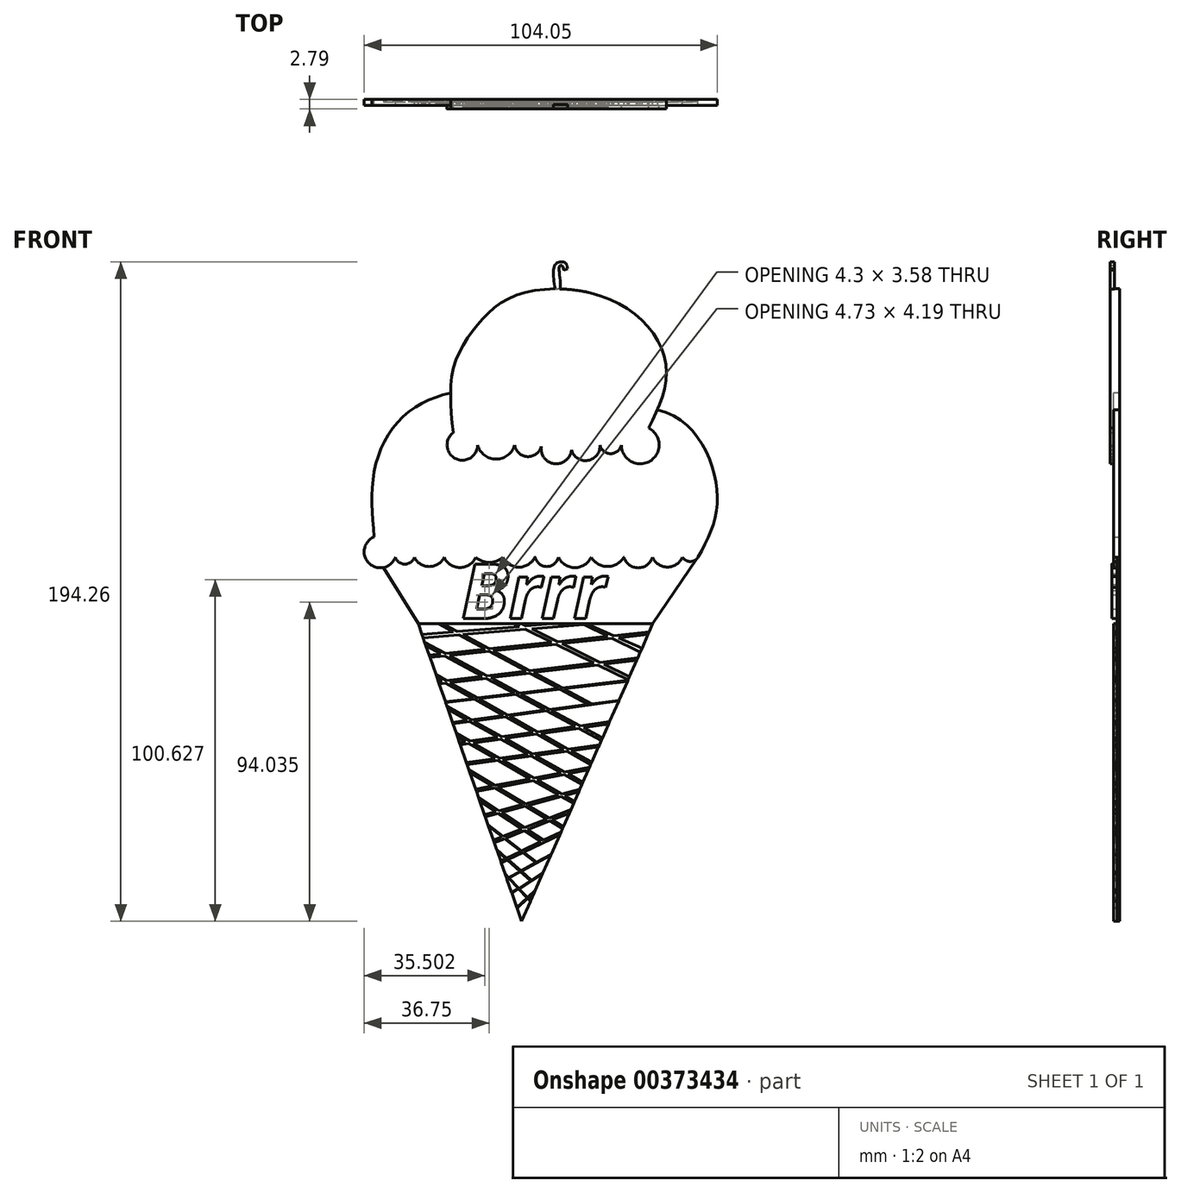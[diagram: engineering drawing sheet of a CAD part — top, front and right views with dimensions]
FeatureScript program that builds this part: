
annotation { "Feature Type Name" : "Feature", "Feature Type Description" : "" }
export const myFeature = defineFeature(function(context is Context, id is Id, definition is map)
    precondition{}
    {
        {
            var Q0;
            Q0=qCreatedBy(makeId("Front.planeOp"),FACE);
            var sketch = newSketch(context, id + "F0", { "sketchPlane" : qUnion([Q0])});
            skLineSegment(sketch, "E0", {"start": v(-30.4, 25.21) * mm, "end": v(0, -62.4) * mm});
            skLineSegment(sketch, "E1", {"start": v(0, -62.4) * mm, "end": v(38.64, 25.21) * mm});
            skLineSegment(sketch, "E2", {"start": v(-30.4, 25.21) * mm, "end": v(38.64, 25.21) * mm});
            skLineSegment(sketch, "E3", {"start": v(-30.4, 25.21) * mm, "end": v(-42.62, 44.84) * mm});
            skLineSegment(sketch, "E4", {"start": v(-42.62, 44.84) * mm, "end": v(51.9, 44.84) * mm});
            skLineSegment(sketch, "E5", {"start": v(51.9, 44.84) * mm, "end": v(38.64, 25.21) * mm});
            skLineSegment(sketch, "E6", {"start": v(-4.74, -48.74) * mm, "end": v(2.58, -56.54) * mm});
            skLineSegment(sketch, "E7", {"start": v(-4.86, -48.38) * mm, "end": v(2.65, -56.4) * mm});
            skLineSegment(sketch, "E8", {"start": v(-7.18, -41.7) * mm, "end": v(4.5, -52.17) * mm});
            skLineSegment(sketch, "E9", {"start": v(-7.38, -41.14) * mm, "end": v(4.5, -51.78) * mm});
            skLineSegment(sketch, "E10", {"start": v(-9.75, -34.3) * mm, "end": v(6.74, -47.12) * mm});
            skLineSegment(sketch, "E11", {"start": v(-9.87, -33.96) * mm, "end": v(6.74, -46.86) * mm});
            skLineSegment(sketch, "E12", {"start": v(-12.3, -26.96) * mm, "end": v(9.29, -41.33) * mm});
            skLineSegment(sketch, "E13", {"start": v(-12.7, -25.8) * mm, "end": v(9.29, -40.44) * mm});
            skLineSegment(sketch, "E14", {"start": v(-15.2, -18.6) * mm, "end": v(12.07, -35.04) * mm});
            skLineSegment(sketch, "E15", {"start": v(-15.46, -17.84) * mm, "end": v(12.27, -34.57) * mm});
            skLineSegment(sketch, "E16", {"start": v(-18.83, -8.15) * mm, "end": v(15.28, -27.74) * mm});
            skLineSegment(sketch, "E17", {"start": v(-19.21, -7.05) * mm, "end": v(15.6, -27.04) * mm});
            skLineSegment(sketch, "E18", {"start": v(-21.66, 0) * mm, "end": v(17.77, -22.1) * mm});
            skLineSegment(sketch, "E19", {"start": v(-22, 1.01) * mm, "end": v(18.06, -21.46) * mm});
            skLineSegment(sketch, "E20", {"start": v(-25.2, 10.22) * mm, "end": v(20.66, -15.56) * mm});
            skLineSegment(sketch, "E21", {"start": v(-28.16, 18.72) * mm, "end": v(23.5, -9.13) * mm});
            skLineSegment(sketch, "E22", {"start": v(-28.54, 19.83) * mm, "end": v(23.81, -8.4) * mm});
            skLineSegment(sketch, "E23", {"start": v(-24.56, 25.21) * mm, "end": v(26.53, -2.24) * mm});
            skLineSegment(sketch, "E24", {"start": v(-23.22, 25.21) * mm, "end": v(26.53, -1.52) * mm});
            skLineSegment(sketch, "E25", {"start": v(-2.21, 25.21) * mm, "end": v(31.38, 8.76) * mm});
            skLineSegment(sketch, "E26", {"start": v(0, 25.21) * mm, "end": v(31.78, 9.65) * mm});
            skLineSegment(sketch, "E27", {"start": v(17.84, 25.21) * mm, "end": v(34.94, 16.83) * mm});
            skLineSegment(sketch, "E28", {"start": v(19.27, 25.21) * mm, "end": v(35.48, 18.06) * mm});
            skLineSegment(sketch, "E29", {"start": v(3.77, -53.84) * mm, "end": v(-1.31, -58.61) * mm});
            skLineSegment(sketch, "E30", {"start": v(4.06, -53.18) * mm, "end": v(-1.41, -58.32) * mm});
            skLineSegment(sketch, "E31", {"start": v(6.21, -48.31) * mm, "end": v(-2.86, -54.17) * mm});
            skLineSegment(sketch, "E32", {"start": v(6.34, -48.03) * mm, "end": v(-2.91, -54) * mm});
            skLineSegment(sketch, "E33", {"start": v(8.6, -42.88) * mm, "end": v(-4.3, -50) * mm});
            skLineSegment(sketch, "E34", {"start": v(8.7, -42.65) * mm, "end": v(-4.35, -49.86) * mm});
            skLineSegment(sketch, "E35", {"start": v(11.6, -36.09) * mm, "end": v(-6.17, -44.6) * mm});
            skLineSegment(sketch, "E36", {"start": v(11.23, -36.94) * mm, "end": v(-6.17, -45.28) * mm});
            skLineSegment(sketch, "E37", {"start": v(14.52, -29.48) * mm, "end": v(-8.3, -38.47) * mm});
            skLineSegment(sketch, "E38", {"start": v(14.02, -30.6) * mm, "end": v(-8.02, -39.28) * mm});
            skLineSegment(sketch, "E39", {"start": v(17.14, -23.52) * mm, "end": v(-10.89, -31.03) * mm});
            skLineSegment(sketch, "E40", {"start": v(16.82, -24.26) * mm, "end": v(-10.89, -31.68) * mm});
            skLineSegment(sketch, "E41", {"start": v(20.35, -16.25) * mm, "end": v(-24.83, 9.14) * mm});
            skLineSegment(sketch, "E42", {"start": v(20, -17.04) * mm, "end": v(-13.5, -23.48) * mm});
            skPoint(sketch, "E42.startSnap0", {"position": v(-1.8, -17.04) * mm});
            skLineSegment(sketch, "E43", {"start": v(19.66, -17.82) * mm, "end": v(-13.5, -24.2) * mm});
            skLineSegment(sketch, "E44", {"start": v(22.92, -10.42) * mm, "end": v(-16.23, -15.63) * mm});
            skLineSegment(sketch, "E45", {"start": v(22.62, -11.11) * mm, "end": v(-16.02, -16.25) * mm});
            skLineSegment(sketch, "E46", {"start": v(25.92, -3.62) * mm, "end": v(-18.28, -9.73) * mm});
            skLineSegment(sketch, "E47", {"start": v(25.6, -4.37) * mm, "end": v(-18.05, -10.4) * mm});
            skLineSegment(sketch, "E48", {"start": v(28.7, 2.7) * mm, "end": v(-20.35, -3.77) * mm});
            skLineSegment(sketch, "E49", {"start": v(-20.18, -4.26) * mm, "end": v(28.61, 2.48) * mm});
            skLineSegment(sketch, "E50", {"start": v(31.17, 8.29) * mm, "end": v(-22.35, 1.98) * mm});
            skLineSegment(sketch, "E51", {"start": v(31.3, 8.57) * mm, "end": v(-22.44, 2.24) * mm});
            skLineSegment(sketch, "E52", {"start": v(34.23, 15.22) * mm, "end": v(-24.5, 8.22) * mm});
            skLineSegment(sketch, "E53", {"start": v(-24.27, 7.53) * mm, "end": v(33.9, 14.47) * mm});
            skLineSegment(sketch, "E54", {"start": v(37.58, 22.81) * mm, "end": v(-27.21, 16) * mm});
            skLineSegment(sketch, "E55", {"start": v(-26.97, 15.3) * mm, "end": v(37.24, 22.04) * mm});
            skLineSegment(sketch, "E56", {"start": v(21.48, 25.21) * mm, "end": v(-28.97, 21.08) * mm});
            skLineSegment(sketch, "E57", {"start": v(-29.32, 22.08) * mm, "end": v(8.91, 25.21) * mm});
            skSolve(sketch);
        }
        {
            var Q0;
            {var subQ0=sQuery(id+"F0.wireOp",EDGE,"E55");var subQ1=sQuery(id+"F0.wireOp",EDGE,"E24");var subQ2=makeQuery(id+"F0.imprint","INTERSECT",VERTEX,{"derivedFrom":[subQ1,subQ0]});Q0=makeQuery(id+"F0.imprint","IMPRINT",FACE,{"disambiguationData":[TD([[makeQuery(id+"F0.imprint","IMPRINT",EDGE,{"disambiguationData":[TD([[subQ2,-1.0]])],"derivedFrom":subQ1}),1.0]])]});}
            var Q1;
            {var subQ0=sQuery(id+"F0.wireOp",EDGE,"E55");var subQ1=sQuery(id+"F0.wireOp",EDGE,"E22");var subQ2=makeQuery(id+"F0.imprint","INTERSECT",VERTEX,{"derivedFrom":[subQ1,subQ0]});Q1=makeQuery(id+"F0.imprint","IMPRINT",FACE,{"disambiguationData":[TD([[makeQuery(id+"F0.imprint","IMPRINT",EDGE,{"disambiguationData":[TD([[subQ2,-1.0]])],"derivedFrom":subQ1}),1.0]])]});}
            var Q2;
            {var subQ0=sQuery(id+"F0.wireOp",EDGE,"E56");var subQ1=sQuery(id+"F0.wireOp",EDGE,"E24");var subQ2=makeQuery(id+"F0.imprint","INTERSECT",VERTEX,{"derivedFrom":[subQ1,subQ0]});Q2=makeQuery(id+"F0.imprint","IMPRINT",FACE,{"disambiguationData":[TD([[makeQuery(id+"F0.imprint","IMPRINT",EDGE,{"disambiguationData":[TD([[subQ2,-1.0]])],"derivedFrom":subQ1}),1.0]])]});}
            var Q3;
            {var subQ1=sQuery(id+"F0.wireOp",EDGE,"E22");var subQ7=sQuery(id+"F0.wireOp",EDGE,"E0");var subQ8=makeQuery(id+"F0.imprint","INTERSECT",VERTEX,{"derivedFrom":[subQ7,subQ1]});Q3=makeQuery(id+"F0.imprint","IMPRINT",FACE,{"disambiguationData":[TD([[makeQuery(id+"F0.imprint","IMPRINT",EDGE,{"disambiguationData":[TD([[subQ8,1.0]])],"derivedFrom":subQ7}),1.0]])]});}
            var Q4;
            {var subQ1=sQuery(id+"F0.wireOp",EDGE,"E1");var subQ7=sQuery(id+"F0.wireOp",EDGE,"E27");var subQ9=makeQuery(id+"F0.imprint","INTERSECT",VERTEX,{"derivedFrom":[subQ1,subQ7]});Q4=makeQuery(id+"F0.imprint","IMPRINT",FACE,{"disambiguationData":[TD([[makeQuery(id+"F0.imprint","IMPRINT",EDGE,{"disambiguationData":[TD([[subQ9,1.0]])],"derivedFrom":subQ1}),1.0]])]});}
            var Q5;
            {var subQ0=sQuery(id+"F0.wireOp",EDGE,"E56");var subQ1=sQuery(id+"F0.wireOp",EDGE,"E26");var subQ2=makeQuery(id+"F0.imprint","INTERSECT",VERTEX,{"derivedFrom":[subQ1,subQ0]});Q5=makeQuery(id+"F0.imprint","IMPRINT",FACE,{"disambiguationData":[TD([[makeQuery(id+"F0.imprint","IMPRINT",EDGE,{"disambiguationData":[TD([[subQ2,-1.0]])],"derivedFrom":subQ1}),1.0]])]});}
            var Q6;
            {var subQ0=sQuery(id+"F0.wireOp",EDGE,"E28");var subQ1=sQuery(id+"F0.wireOp",EDGE,"E1");var subQ2=makeQuery(id+"F0.imprint","INTERSECT",VERTEX,{"derivedFrom":[subQ1,subQ0]});Q6=makeQuery(id+"F0.imprint","IMPRINT",FACE,{"disambiguationData":[TD([[makeQuery(id+"F0.imprint","IMPRINT",EDGE,{"disambiguationData":[TD([[subQ2,-1.0]])],"derivedFrom":subQ1}),1.0]])]});}
            var Q7;
            {var subQ0=sQuery(id+"F0.wireOp",EDGE,"E26");var subQ1=sQuery(id+"F0.wireOp",EDGE,"E1");var subQ2=makeQuery(id+"F0.imprint","INTERSECT",VERTEX,{"derivedFrom":[subQ1,subQ0]});Q7=makeQuery(id+"F0.imprint","IMPRINT",FACE,{"disambiguationData":[TD([[makeQuery(id+"F0.imprint","IMPRINT",EDGE,{"disambiguationData":[TD([[subQ2,-1.0]])],"derivedFrom":subQ1}),1.0]])]});}
            var Q8;
            {var subQ1=sQuery(id+"F0.wireOp",EDGE,"E1");var subQ7=sQuery(id+"F0.wireOp",EDGE,"E25");var subQ9=makeQuery(id+"F0.imprint","INTERSECT",VERTEX,{"derivedFrom":[subQ1,subQ7]});Q8=makeQuery(id+"F0.imprint","IMPRINT",FACE,{"disambiguationData":[TD([[makeQuery(id+"F0.imprint","IMPRINT",EDGE,{"disambiguationData":[TD([[subQ9,1.0]])],"derivedFrom":subQ1}),1.0]])]});}
            var Q9;
            {var subQ0=sQuery(id+"F0.wireOp",EDGE,"E48");var subQ1=sQuery(id+"F0.wireOp",EDGE,"E1");var subQ2=makeQuery(id+"F0.imprint","INTERSECT",VERTEX,{"derivedFrom":[subQ1,subQ0]});Q9=makeQuery(id+"F0.imprint","IMPRINT",FACE,{"disambiguationData":[TD([[makeQuery(id+"F0.imprint","IMPRINT",EDGE,{"disambiguationData":[TD([[subQ2,-1.0]])],"derivedFrom":subQ1}),1.0]])]});}
            var Q10;
            {var subQ0=sQuery(id+"F0.wireOp",EDGE,"E50");var subQ1=sQuery(id+"F0.wireOp",EDGE,"E22");var subQ2=makeQuery(id+"F0.imprint","INTERSECT",VERTEX,{"derivedFrom":[subQ1,subQ0]});Q10=makeQuery(id+"F0.imprint","IMPRINT",FACE,{"disambiguationData":[TD([[makeQuery(id+"F0.imprint","IMPRINT",EDGE,{"disambiguationData":[TD([[subQ2,-1.0]])],"derivedFrom":subQ1}),1.0]])]});}
            var Q11;
            {var subQ0=sQuery(id+"F0.wireOp",EDGE,"E53");var subQ1=sQuery(id+"F0.wireOp",EDGE,"E22");var subQ2=makeQuery(id+"F0.imprint","INTERSECT",VERTEX,{"derivedFrom":[subQ1,subQ0]});Q11=makeQuery(id+"F0.imprint","IMPRINT",FACE,{"disambiguationData":[TD([[makeQuery(id+"F0.imprint","IMPRINT",EDGE,{"disambiguationData":[TD([[subQ2,-1.0]])],"derivedFrom":subQ1}),1.0]])]});}
            var Q12;
            {var subQ0=sQuery(id+"F0.wireOp",EDGE,"E53");var subQ1=sQuery(id+"F0.wireOp",EDGE,"E20");var subQ2=makeQuery(id+"F0.imprint","INTERSECT",VERTEX,{"derivedFrom":[subQ1,subQ0]});Q12=makeQuery(id+"F0.imprint","IMPRINT",FACE,{"disambiguationData":[TD([[makeQuery(id+"F0.imprint","IMPRINT",EDGE,{"disambiguationData":[TD([[subQ2,-1.0]])],"derivedFrom":subQ1}),1.0]])]});}
            var Q13;
            {var subQ0=sQuery(id+"F0.wireOp",EDGE,"E50");var subQ1=sQuery(id+"F0.wireOp",EDGE,"E20");var subQ2=makeQuery(id+"F0.imprint","INTERSECT",VERTEX,{"derivedFrom":[subQ1,subQ0]});Q13=makeQuery(id+"F0.imprint","IMPRINT",FACE,{"disambiguationData":[TD([[makeQuery(id+"F0.imprint","IMPRINT",EDGE,{"disambiguationData":[TD([[subQ2,-1.0]])],"derivedFrom":subQ1}),1.0]])]});}
            var Q14;
            {var subQ0=sQuery(id+"F0.wireOp",EDGE,"E49");var subQ1=sQuery(id+"F0.wireOp",EDGE,"E20");var subQ2=makeQuery(id+"F0.imprint","INTERSECT",VERTEX,{"derivedFrom":[subQ1,subQ0]});Q14=makeQuery(id+"F0.imprint","IMPRINT",FACE,{"disambiguationData":[TD([[makeQuery(id+"F0.imprint","IMPRINT",EDGE,{"disambiguationData":[TD([[subQ2,-1.0]])],"derivedFrom":subQ1}),1.0]])]});}
            var Q15;
            {var subQ1=sQuery(id+"F0.wireOp",EDGE,"E1");var subQ7=sQuery(id+"F0.wireOp",EDGE,"E23");var subQ9=makeQuery(id+"F0.imprint","INTERSECT",VERTEX,{"derivedFrom":[subQ1,subQ7]});Q15=makeQuery(id+"F0.imprint","IMPRINT",FACE,{"disambiguationData":[TD([[makeQuery(id+"F0.imprint","IMPRINT",EDGE,{"disambiguationData":[TD([[subQ9,1.0]])],"derivedFrom":subQ1}),1.0]])]});}
            var Q16;
            {var subQ0=sQuery(id+"F0.wireOp",EDGE,"E21");var subQ1=sQuery(id+"F0.wireOp",EDGE,"E1");var subQ2=makeQuery(id+"F0.imprint","INTERSECT",VERTEX,{"derivedFrom":[subQ1,subQ0]});Q16=makeQuery(id+"F0.imprint","IMPRINT",FACE,{"disambiguationData":[TD([[makeQuery(id+"F0.imprint","IMPRINT",EDGE,{"disambiguationData":[TD([[subQ2,1.0]])],"derivedFrom":subQ1}),1.0]])]});}
            var Q17;
            {var subQ0=sQuery(id+"F0.wireOp",EDGE,"E47");var subQ1=sQuery(id+"F0.wireOp",EDGE,"E19");var subQ2=makeQuery(id+"F0.imprint","INTERSECT",VERTEX,{"derivedFrom":[subQ1,subQ0]});Q17=makeQuery(id+"F0.imprint","IMPRINT",FACE,{"disambiguationData":[TD([[makeQuery(id+"F0.imprint","IMPRINT",EDGE,{"disambiguationData":[TD([[subQ2,-1.0]])],"derivedFrom":subQ1}),1.0]])]});}
            var Q18;
            {var subQ0=sQuery(id+"F0.wireOp",EDGE,"E49");var subQ1=sQuery(id+"F0.wireOp",EDGE,"E19");var subQ2=makeQuery(id+"F0.imprint","INTERSECT",VERTEX,{"derivedFrom":[subQ1,subQ0]});Q18=makeQuery(id+"F0.imprint","IMPRINT",FACE,{"disambiguationData":[TD([[makeQuery(id+"F0.imprint","IMPRINT",EDGE,{"disambiguationData":[TD([[subQ2,-1.0]])],"derivedFrom":subQ1}),1.0]])]});}
            var Q19;
            {var subQ5=sQuery(id+"F0.wireOp",EDGE,"E19");var subQ7=sQuery(id+"F0.wireOp",EDGE,"E0");var subQ8=makeQuery(id+"F0.imprint","INTERSECT",VERTEX,{"derivedFrom":[subQ7,subQ5]});Q19=makeQuery(id+"F0.imprint","IMPRINT",FACE,{"disambiguationData":[TD([[makeQuery(id+"F0.imprint","IMPRINT",EDGE,{"disambiguationData":[TD([[subQ8,1.0]])],"derivedFrom":subQ7}),1.0]])]});}
            var Q20;
            {var subQ5=sQuery(id+"F0.wireOp",EDGE,"E17");var subQ7=sQuery(id+"F0.wireOp",EDGE,"E0");var subQ8=makeQuery(id+"F0.imprint","INTERSECT",VERTEX,{"derivedFrom":[subQ7,subQ5]});Q20=makeQuery(id+"F0.imprint","IMPRINT",FACE,{"disambiguationData":[TD([[makeQuery(id+"F0.imprint","IMPRINT",EDGE,{"disambiguationData":[TD([[subQ8,1.0]])],"derivedFrom":subQ7}),1.0]])]});}
            var Q21;
            {var subQ0=sQuery(id+"F0.wireOp",EDGE,"E47");var subQ1=sQuery(id+"F0.wireOp",EDGE,"E17");var subQ2=makeQuery(id+"F0.imprint","INTERSECT",VERTEX,{"derivedFrom":[subQ1,subQ0]});Q21=makeQuery(id+"F0.imprint","IMPRINT",FACE,{"disambiguationData":[TD([[makeQuery(id+"F0.imprint","IMPRINT",EDGE,{"disambiguationData":[TD([[subQ2,-1.0]])],"derivedFrom":subQ1}),1.0]])]});}
            var Q22;
            {var subQ0=sQuery(id+"F0.wireOp",EDGE,"E45");var subQ1=sQuery(id+"F0.wireOp",EDGE,"E17");var subQ2=makeQuery(id+"F0.imprint","INTERSECT",VERTEX,{"derivedFrom":[subQ1,subQ0]});Q22=makeQuery(id+"F0.imprint","IMPRINT",FACE,{"disambiguationData":[TD([[makeQuery(id+"F0.imprint","IMPRINT",EDGE,{"disambiguationData":[TD([[subQ2,-1.0]])],"derivedFrom":subQ1}),1.0]])]});}
            var Q23;
            {var subQ1=sQuery(id+"F0.wireOp",EDGE,"E1");var subQ5=sQuery(id+"F0.wireOp",EDGE,"E41");var subQ6=makeQuery(id+"F0.imprint","INTERSECT",VERTEX,{"derivedFrom":[subQ1,subQ5]});Q23=makeQuery(id+"F0.imprint","IMPRINT",FACE,{"disambiguationData":[TD([[makeQuery(id+"F0.imprint","IMPRINT",EDGE,{"disambiguationData":[TD([[subQ6,1.0]])],"derivedFrom":subQ1}),1.0]])]});}
            var Q24;
            {var subQ0=sQuery(id+"F0.wireOp",EDGE,"E18");var subQ1=sQuery(id+"F0.wireOp",EDGE,"E1");var subQ2=makeQuery(id+"F0.imprint","INTERSECT",VERTEX,{"derivedFrom":[subQ1,subQ0]});Q24=makeQuery(id+"F0.imprint","IMPRINT",FACE,{"disambiguationData":[TD([[makeQuery(id+"F0.imprint","IMPRINT",EDGE,{"disambiguationData":[TD([[subQ2,1.0]])],"derivedFrom":subQ1}),1.0]])]});}
            var Q25;
            {var subQ0=sQuery(id+"F0.wireOp",EDGE,"E43");var subQ1=sQuery(id+"F0.wireOp",EDGE,"E15");var subQ2=makeQuery(id+"F0.imprint","INTERSECT",VERTEX,{"derivedFrom":[subQ1,subQ0]});Q25=makeQuery(id+"F0.imprint","IMPRINT",FACE,{"disambiguationData":[TD([[makeQuery(id+"F0.imprint","IMPRINT",EDGE,{"disambiguationData":[TD([[subQ2,-1.0]])],"derivedFrom":subQ1}),1.0]])]});}
            var Q26;
            {var subQ1=sQuery(id+"F0.wireOp",EDGE,"E13");var subQ5=sQuery(id+"F0.wireOp",EDGE,"E0");var subQ6=makeQuery(id+"F0.imprint","INTERSECT",VERTEX,{"derivedFrom":[subQ5,subQ1]});Q26=makeQuery(id+"F0.imprint","IMPRINT",FACE,{"disambiguationData":[TD([[makeQuery(id+"F0.imprint","IMPRINT",EDGE,{"disambiguationData":[TD([[subQ6,1.0]])],"derivedFrom":subQ5}),1.0]])]});}
            var Q27;
            {var subQ0=sQuery(id+"F0.wireOp",EDGE,"E15");var subQ1=sQuery(id+"F0.wireOp",EDGE,"E0");var subQ2=makeQuery(id+"F0.imprint","INTERSECT",VERTEX,{"derivedFrom":[subQ1,subQ0]});Q27=makeQuery(id+"F0.imprint","IMPRINT",FACE,{"disambiguationData":[TD([[makeQuery(id+"F0.imprint","IMPRINT",EDGE,{"disambiguationData":[TD([[subQ2,1.0]])],"derivedFrom":subQ1}),1.0]])]});}
            var Q28;
            {var subQ0=sQuery(id+"F0.wireOp",EDGE,"E40");var subQ1=sQuery(id+"F0.wireOp",EDGE,"E13");var subQ2=makeQuery(id+"F0.imprint","INTERSECT",VERTEX,{"derivedFrom":[subQ1,subQ0]});Q28=makeQuery(id+"F0.imprint","IMPRINT",FACE,{"disambiguationData":[TD([[makeQuery(id+"F0.imprint","IMPRINT",EDGE,{"disambiguationData":[TD([[subQ2,-1.0]])],"derivedFrom":subQ1}),1.0]])]});}
            var Q29;
            {var subQ0=sQuery(id+"F0.wireOp",EDGE,"E16");var subQ1=sQuery(id+"F0.wireOp",EDGE,"E1");var subQ2=makeQuery(id+"F0.imprint","INTERSECT",VERTEX,{"derivedFrom":[subQ1,subQ0]});Q29=makeQuery(id+"F0.imprint","IMPRINT",FACE,{"disambiguationData":[TD([[makeQuery(id+"F0.imprint","IMPRINT",EDGE,{"disambiguationData":[TD([[subQ2,1.0]])],"derivedFrom":subQ1}),1.0]])]});}
            var Q30;
            {var subQ5=sQuery(id+"F0.wireOp",EDGE,"E1");var subQ7=sQuery(id+"F0.wireOp",EDGE,"E14");var subQ8=makeQuery(id+"F0.imprint","INTERSECT",VERTEX,{"derivedFrom":[subQ5,subQ7]});Q30=makeQuery(id+"F0.imprint","IMPRINT",FACE,{"disambiguationData":[TD([[makeQuery(id+"F0.imprint","IMPRINT",EDGE,{"disambiguationData":[TD([[subQ8,1.0]])],"derivedFrom":subQ5}),1.0]])]});}
            var Q31;
            {var subQ0=sQuery(id+"F0.wireOp",EDGE,"E38");var subQ1=sQuery(id+"F0.wireOp",EDGE,"E11");var subQ2=makeQuery(id+"F0.imprint","INTERSECT",VERTEX,{"derivedFrom":[subQ1,subQ0]});Q31=makeQuery(id+"F0.imprint","IMPRINT",FACE,{"disambiguationData":[TD([[makeQuery(id+"F0.imprint","IMPRINT",EDGE,{"disambiguationData":[TD([[subQ2,-1.0]])],"derivedFrom":subQ1}),1.0]])]});}
            var Q32;
            {var subQ1=sQuery(id+"F0.wireOp",EDGE,"E11");var subQ7=sQuery(id+"F0.wireOp",EDGE,"E0");var subQ8=makeQuery(id+"F0.imprint","INTERSECT",VERTEX,{"derivedFrom":[subQ7,subQ1]});Q32=makeQuery(id+"F0.imprint","IMPRINT",FACE,{"disambiguationData":[TD([[makeQuery(id+"F0.imprint","IMPRINT",EDGE,{"disambiguationData":[TD([[subQ8,1.0]])],"derivedFrom":subQ7}),1.0]])]});}
            var Q33;
            {var subQ5=sQuery(id+"F0.wireOp",EDGE,"E9");var subQ6=sQuery(id+"F0.wireOp",EDGE,"E0");var subQ7=makeQuery(id+"F0.imprint","INTERSECT",VERTEX,{"derivedFrom":[subQ6,subQ5]});Q33=makeQuery(id+"F0.imprint","IMPRINT",FACE,{"disambiguationData":[TD([[makeQuery(id+"F0.imprint","IMPRINT",EDGE,{"disambiguationData":[TD([[subQ7,1.0]])],"derivedFrom":subQ6}),1.0]])]});}
            var Q34;
            {var subQ1=sQuery(id+"F0.wireOp",EDGE,"E1");var subQ7=sQuery(id+"F0.wireOp",EDGE,"E12");var subQ8=makeQuery(id+"F0.imprint","INTERSECT",VERTEX,{"derivedFrom":[subQ1,subQ7]});Q34=makeQuery(id+"F0.imprint","IMPRINT",FACE,{"disambiguationData":[TD([[makeQuery(id+"F0.imprint","IMPRINT",EDGE,{"disambiguationData":[TD([[subQ8,1.0]])],"derivedFrom":subQ1}),1.0]])]});}
            var Q35;
            {var subQ0=sQuery(id+"F0.wireOp",EDGE,"E36");var subQ1=sQuery(id+"F0.wireOp",EDGE,"E9");var subQ2=makeQuery(id+"F0.imprint","INTERSECT",VERTEX,{"derivedFrom":[subQ1,subQ0]});Q35=makeQuery(id+"F0.imprint","IMPRINT",FACE,{"disambiguationData":[TD([[makeQuery(id+"F0.imprint","IMPRINT",EDGE,{"disambiguationData":[TD([[subQ2,-1.0]])],"derivedFrom":subQ1}),1.0]])]});}
            var Q36;
            {var subQ1=sQuery(id+"F0.wireOp",EDGE,"E1");var subQ7=sQuery(id+"F0.wireOp",EDGE,"E10");var subQ8=makeQuery(id+"F0.imprint","INTERSECT",VERTEX,{"derivedFrom":[subQ1,subQ7]});Q36=makeQuery(id+"F0.imprint","IMPRINT",FACE,{"disambiguationData":[TD([[makeQuery(id+"F0.imprint","IMPRINT",EDGE,{"disambiguationData":[TD([[subQ8,1.0]])],"derivedFrom":subQ1}),1.0]])]});}
            var Q37;
            {var subQ0=sQuery(id+"F0.wireOp",EDGE,"E33");var subQ1=sQuery(id+"F0.wireOp",EDGE,"E7");var subQ2=makeQuery(id+"F0.imprint","INTERSECT",VERTEX,{"derivedFrom":[subQ1,subQ0]});Q37=makeQuery(id+"F0.imprint","IMPRINT",FACE,{"disambiguationData":[TD([[makeQuery(id+"F0.imprint","IMPRINT",EDGE,{"disambiguationData":[TD([[subQ2,-1.0]])],"derivedFrom":subQ1}),1.0]])]});}
            var Q38;
            {var subQ1=sQuery(id+"F0.wireOp",EDGE,"E1");var subQ7=sQuery(id+"F0.wireOp",EDGE,"E8");var subQ8=makeQuery(id+"F0.imprint","INTERSECT",VERTEX,{"derivedFrom":[subQ1,subQ7]});Q38=makeQuery(id+"F0.imprint","IMPRINT",FACE,{"disambiguationData":[TD([[makeQuery(id+"F0.imprint","IMPRINT",EDGE,{"disambiguationData":[TD([[subQ8,1.0]])],"derivedFrom":subQ1}),1.0]])]});}
            var Q39;
            {var subQ0=sQuery(id+"F0.wireOp",EDGE,"E30");var subQ1=sQuery(id+"F0.wireOp",EDGE,"E0");var subQ2=makeQuery(id+"F0.imprint","INTERSECT",VERTEX,{"derivedFrom":[subQ1,subQ0]});Q39=makeQuery(id+"F0.imprint","IMPRINT",FACE,{"disambiguationData":[TD([[makeQuery(id+"F0.imprint","IMPRINT",EDGE,{"disambiguationData":[TD([[subQ2,1.0]])],"derivedFrom":subQ1}),1.0]])]});}
            var Q40;
            {var subQ0=sQuery(id+"F0.wireOp",EDGE,"E1");var subQ1=sQuery(id+"F0.wireOp",EDGE,"E0");var subQ2=makeQuery(id+"F0.imprint","INTERSECT",VERTEX,{"derivedFrom":[subQ1,subQ0]});Q40=makeQuery(id+"F0.imprint","IMPRINT",FACE,{"disambiguationData":[TD([[makeQuery(id+"F0.imprint","IMPRINT",EDGE,{"disambiguationData":[TD([[subQ2,1.0]])],"derivedFrom":subQ1}),1.0]])]});}
            var Q41;
            {var subQ0=sQuery(id+"F0.wireOp",EDGE,"E44");var subQ1=sQuery(id+"F0.wireOp",EDGE,"E0");var subQ2=makeQuery(id+"F0.imprint","INTERSECT",VERTEX,{"derivedFrom":[subQ1,subQ0]});Q41=makeQuery(id+"F0.imprint","IMPRINT",FACE,{"disambiguationData":[TD([[makeQuery(id+"F0.imprint","IMPRINT",EDGE,{"disambiguationData":[TD([[subQ2,1.0]])],"derivedFrom":subQ1}),1.0]])]});}
            var Q42;
            {var subQ0=sQuery(id+"F0.wireOp",EDGE,"E18");var subQ1=sQuery(id+"F0.wireOp",EDGE,"E0");var subQ2=makeQuery(id+"F0.imprint","INTERSECT",VERTEX,{"derivedFrom":[subQ1,subQ0]});Q42=makeQuery(id+"F0.imprint","IMPRINT",FACE,{"disambiguationData":[TD([[makeQuery(id+"F0.imprint","IMPRINT",EDGE,{"disambiguationData":[TD([[subQ2,-1.0]])],"derivedFrom":subQ1}),1.0]])]});}
            var Q43;
            {var subQ0=sQuery(id+"F0.wireOp",EDGE,"E51");var subQ1=sQuery(id+"F0.wireOp",EDGE,"E0");var subQ2=makeQuery(id+"F0.imprint","INTERSECT",VERTEX,{"derivedFrom":[subQ1,subQ0]});Q43=makeQuery(id+"F0.imprint","IMPRINT",FACE,{"disambiguationData":[TD([[makeQuery(id+"F0.imprint","IMPRINT",EDGE,{"disambiguationData":[TD([[subQ2,1.0]])],"derivedFrom":subQ1}),1.0]])]});}
            var Q44;
            {var subQ1=sQuery(id+"F0.wireOp",EDGE,"E20");var subQ7=sQuery(id+"F0.wireOp",EDGE,"E0");var subQ8=makeQuery(id+"F0.imprint","INTERSECT",VERTEX,{"derivedFrom":[subQ7,subQ1]});Q44=makeQuery(id+"F0.imprint","IMPRINT",FACE,{"disambiguationData":[TD([[makeQuery(id+"F0.imprint","IMPRINT",EDGE,{"disambiguationData":[TD([[subQ8,1.0]])],"derivedFrom":subQ7}),1.0]])]});}
            var Q45;
            {var subQ0=sQuery(id+"F0.wireOp",EDGE,"E24");var subQ1=sQuery(id+"F0.wireOp",EDGE,"E2");var subQ2=makeQuery(id+"F0.imprint","INTERSECT",VERTEX,{"derivedFrom":[subQ1,subQ0]});Q45=makeQuery(id+"F0.imprint","IMPRINT",FACE,{"disambiguationData":[TD([[makeQuery(id+"F0.imprint","IMPRINT",EDGE,{"disambiguationData":[TD([[subQ2,-1.0]])],"derivedFrom":subQ1}),-1.0]])]});}
            var Q46;
            {var subQ3=sQuery(id+"F0.wireOp",EDGE,"E28");var subQ5=sQuery(id+"F0.wireOp",EDGE,"E56");var subQ6=makeQuery(id+"F0.imprint","INTERSECT",VERTEX,{"derivedFrom":[subQ3,subQ5]});Q46=makeQuery(id+"F0.imprint","IMPRINT",FACE,{"disambiguationData":[TD([[makeQuery(id+"F0.imprint","IMPRINT",EDGE,{"disambiguationData":[TD([[subQ6,-1.0]])],"derivedFrom":subQ3}),1.0]])]});}
            var Q47;
            {var subQ0=sQuery(id+"F0.wireOp",EDGE,"E23");var subQ1=sQuery(id+"F0.wireOp",EDGE,"E1");var subQ2=makeQuery(id+"F0.imprint","INTERSECT",VERTEX,{"derivedFrom":[subQ1,subQ0]});Q47=makeQuery(id+"F0.imprint","IMPRINT",FACE,{"disambiguationData":[TD([[makeQuery(id+"F0.imprint","IMPRINT",EDGE,{"disambiguationData":[TD([[subQ2,-1.0]])],"derivedFrom":subQ1}),1.0]])]});}
            var Q48;
            {var subQ0=sQuery(id+"F0.wireOp",EDGE,"E22");var subQ1=sQuery(id+"F0.wireOp",EDGE,"E1");var subQ2=makeQuery(id+"F0.imprint","INTERSECT",VERTEX,{"derivedFrom":[subQ1,subQ0]});Q48=makeQuery(id+"F0.imprint","IMPRINT",FACE,{"disambiguationData":[TD([[makeQuery(id+"F0.imprint","IMPRINT",EDGE,{"disambiguationData":[TD([[subQ2,-1.0]])],"derivedFrom":subQ1}),1.0]])]});}
            var Q49;
            {var subQ0=sQuery(id+"F0.wireOp",EDGE,"E20");var subQ1=sQuery(id+"F0.wireOp",EDGE,"E1");var subQ2=makeQuery(id+"F0.imprint","INTERSECT",VERTEX,{"derivedFrom":[subQ1,subQ0]});Q49=makeQuery(id+"F0.imprint","IMPRINT",FACE,{"disambiguationData":[TD([[makeQuery(id+"F0.imprint","IMPRINT",EDGE,{"disambiguationData":[TD([[subQ2,-1.0]])],"derivedFrom":subQ1}),1.0]])]});}
            var Q50;
            {var subQ0=sQuery(id+"F0.wireOp",EDGE,"E19");var subQ1=sQuery(id+"F0.wireOp",EDGE,"E1");var subQ2=makeQuery(id+"F0.imprint","INTERSECT",VERTEX,{"derivedFrom":[subQ1,subQ0]});Q50=makeQuery(id+"F0.imprint","IMPRINT",FACE,{"disambiguationData":[TD([[makeQuery(id+"F0.imprint","IMPRINT",EDGE,{"disambiguationData":[TD([[subQ2,-1.0]])],"derivedFrom":subQ1}),1.0]])]});}
            var Q51;
            {var subQ0=sQuery(id+"F0.wireOp",EDGE,"E17");var subQ1=sQuery(id+"F0.wireOp",EDGE,"E1");var subQ2=makeQuery(id+"F0.imprint","INTERSECT",VERTEX,{"derivedFrom":[subQ1,subQ0]});Q51=makeQuery(id+"F0.imprint","IMPRINT",FACE,{"disambiguationData":[TD([[makeQuery(id+"F0.imprint","IMPRINT",EDGE,{"disambiguationData":[TD([[subQ2,-1.0]])],"derivedFrom":subQ1}),1.0]])]});}
            var Q52;
            {var subQ0=sQuery(id+"F0.wireOp",EDGE,"E15");var subQ1=sQuery(id+"F0.wireOp",EDGE,"E1");var subQ2=makeQuery(id+"F0.imprint","INTERSECT",VERTEX,{"derivedFrom":[subQ1,subQ0]});Q52=makeQuery(id+"F0.imprint","IMPRINT",FACE,{"disambiguationData":[TD([[makeQuery(id+"F0.imprint","IMPRINT",EDGE,{"disambiguationData":[TD([[subQ2,-1.0]])],"derivedFrom":subQ1}),1.0]])]});}
            var Q53;
            {var subQ0=sQuery(id+"F0.wireOp",EDGE,"E12");var subQ1=sQuery(id+"F0.wireOp",EDGE,"E1");var subQ2=makeQuery(id+"F0.imprint","INTERSECT",VERTEX,{"derivedFrom":[subQ1,subQ0]});Q53=makeQuery(id+"F0.imprint","IMPRINT",FACE,{"disambiguationData":[TD([[makeQuery(id+"F0.imprint","IMPRINT",EDGE,{"disambiguationData":[TD([[subQ2,-1.0]])],"derivedFrom":subQ1}),1.0]])]});}
            var Q54;
            {var subQ0=sQuery(id+"F0.wireOp",EDGE,"E10");var subQ1=sQuery(id+"F0.wireOp",EDGE,"E1");var subQ2=makeQuery(id+"F0.imprint","INTERSECT",VERTEX,{"derivedFrom":[subQ1,subQ0]});Q54=makeQuery(id+"F0.imprint","IMPRINT",FACE,{"disambiguationData":[TD([[makeQuery(id+"F0.imprint","IMPRINT",EDGE,{"disambiguationData":[TD([[subQ2,-1.0]])],"derivedFrom":subQ1}),1.0]])]});}
            var Q55;
            {var subQ0=sQuery(id+"F0.wireOp",EDGE,"E8");var subQ1=sQuery(id+"F0.wireOp",EDGE,"E1");var subQ2=makeQuery(id+"F0.imprint","INTERSECT",VERTEX,{"derivedFrom":[subQ1,subQ0]});Q55=makeQuery(id+"F0.imprint","IMPRINT",FACE,{"disambiguationData":[TD([[makeQuery(id+"F0.imprint","IMPRINT",EDGE,{"disambiguationData":[TD([[subQ2,-1.0]])],"derivedFrom":subQ1}),1.0]])]});}
            var Q56;
            {var subQ0=sQuery(id+"F0.wireOp",EDGE,"E7");var subQ1=sQuery(id+"F0.wireOp",EDGE,"E1");var subQ2=makeQuery(id+"F0.imprint","INTERSECT",VERTEX,{"derivedFrom":[subQ1,subQ0]});Q56=makeQuery(id+"F0.imprint","IMPRINT",FACE,{"disambiguationData":[TD([[makeQuery(id+"F0.imprint","IMPRINT",EDGE,{"disambiguationData":[TD([[subQ2,-1.0]])],"derivedFrom":subQ1}),1.0]])]});}
            var Q57;
            {var subQ0=sQuery(id+"F0.wireOp",EDGE,"E32");var subQ1=sQuery(id+"F0.wireOp",EDGE,"E0");var subQ2=makeQuery(id+"F0.imprint","INTERSECT",VERTEX,{"derivedFrom":[subQ1,subQ0]});Q57=makeQuery(id+"F0.imprint","IMPRINT",FACE,{"disambiguationData":[TD([[makeQuery(id+"F0.imprint","IMPRINT",EDGE,{"disambiguationData":[TD([[subQ2,1.0]])],"derivedFrom":subQ1}),1.0]])]});}
            var Q58;
            {var subQ0=sQuery(id+"F0.wireOp",EDGE,"E6");var subQ1=sQuery(id+"F0.wireOp",EDGE,"E0");var subQ2=makeQuery(id+"F0.imprint","INTERSECT",VERTEX,{"derivedFrom":[subQ1,subQ0]});Q58=makeQuery(id+"F0.imprint","IMPRINT",FACE,{"disambiguationData":[TD([[makeQuery(id+"F0.imprint","IMPRINT",EDGE,{"disambiguationData":[TD([[subQ2,-1.0]])],"derivedFrom":subQ1}),1.0]])]});}
            var Q59;
            {var subQ1=sQuery(id+"F0.wireOp",EDGE,"E7");var subQ7=sQuery(id+"F0.wireOp",EDGE,"E0");var subQ8=makeQuery(id+"F0.imprint","INTERSECT",VERTEX,{"derivedFrom":[subQ7,subQ1]});Q59=makeQuery(id+"F0.imprint","IMPRINT",FACE,{"disambiguationData":[TD([[makeQuery(id+"F0.imprint","IMPRINT",EDGE,{"disambiguationData":[TD([[subQ8,1.0]])],"derivedFrom":subQ7}),1.0]])]});}
            var Q60;
            {var subQ0=sQuery(id+"F0.wireOp",EDGE,"E8");var subQ1=sQuery(id+"F0.wireOp",EDGE,"E0");var subQ2=makeQuery(id+"F0.imprint","INTERSECT",VERTEX,{"derivedFrom":[subQ1,subQ0]});Q60=makeQuery(id+"F0.imprint","IMPRINT",FACE,{"disambiguationData":[TD([[makeQuery(id+"F0.imprint","IMPRINT",EDGE,{"disambiguationData":[TD([[subQ2,-1.0]])],"derivedFrom":subQ1}),1.0]])]});}
            var Q61;
            {var subQ0=sQuery(id+"F0.wireOp",EDGE,"E10");var subQ1=sQuery(id+"F0.wireOp",EDGE,"E0");var subQ2=makeQuery(id+"F0.imprint","INTERSECT",VERTEX,{"derivedFrom":[subQ1,subQ0]});Q61=makeQuery(id+"F0.imprint","IMPRINT",FACE,{"disambiguationData":[TD([[makeQuery(id+"F0.imprint","IMPRINT",EDGE,{"disambiguationData":[TD([[subQ2,-1.0]])],"derivedFrom":subQ1}),1.0]])]});}
            var Q62;
            {var subQ0=sQuery(id+"F0.wireOp",EDGE,"E12");var subQ1=sQuery(id+"F0.wireOp",EDGE,"E0");var subQ2=makeQuery(id+"F0.imprint","INTERSECT",VERTEX,{"derivedFrom":[subQ1,subQ0]});Q62=makeQuery(id+"F0.imprint","IMPRINT",FACE,{"disambiguationData":[TD([[makeQuery(id+"F0.imprint","IMPRINT",EDGE,{"disambiguationData":[TD([[subQ2,-1.0]])],"derivedFrom":subQ1}),1.0]])]});}
            var Q63;
            {var subQ0=sQuery(id+"F0.wireOp",EDGE,"E14");var subQ1=sQuery(id+"F0.wireOp",EDGE,"E0");var subQ2=makeQuery(id+"F0.imprint","INTERSECT",VERTEX,{"derivedFrom":[subQ1,subQ0]});Q63=makeQuery(id+"F0.imprint","IMPRINT",FACE,{"disambiguationData":[TD([[makeQuery(id+"F0.imprint","IMPRINT",EDGE,{"disambiguationData":[TD([[subQ2,-1.0]])],"derivedFrom":subQ1}),1.0]])]});}
            var Q64;
            {var subQ0=sQuery(id+"F0.wireOp",EDGE,"E16");var subQ1=sQuery(id+"F0.wireOp",EDGE,"E0");var subQ2=makeQuery(id+"F0.imprint","INTERSECT",VERTEX,{"derivedFrom":[subQ1,subQ0]});Q64=makeQuery(id+"F0.imprint","IMPRINT",FACE,{"disambiguationData":[TD([[makeQuery(id+"F0.imprint","IMPRINT",EDGE,{"disambiguationData":[TD([[subQ2,-1.0]])],"derivedFrom":subQ1}),1.0]])]});}
            var Q65;
            {var subQ0=sQuery(id+"F0.wireOp",EDGE,"E41");var subQ1=sQuery(id+"F0.wireOp",EDGE,"E0");var subQ2=makeQuery(id+"F0.imprint","INTERSECT",VERTEX,{"derivedFrom":[subQ1,subQ0]});Q65=makeQuery(id+"F0.imprint","IMPRINT",FACE,{"disambiguationData":[TD([[makeQuery(id+"F0.imprint","IMPRINT",EDGE,{"disambiguationData":[TD([[subQ2,-1.0]])],"derivedFrom":subQ1}),1.0]])]});}
            var Q66;
            {var subQ0=sQuery(id+"F0.wireOp",EDGE,"E2");var subQ5=sQuery(id+"F0.wireOp",EDGE,"E23");var subQ6=makeQuery(id+"F0.imprint","INTERSECT",VERTEX,{"derivedFrom":[subQ0,subQ5]});Q66=makeQuery(id+"F0.imprint","IMPRINT",FACE,{"disambiguationData":[TD([[makeQuery(id+"F0.imprint","IMPRINT",EDGE,{"disambiguationData":[TD([[subQ6,-1.0]])],"derivedFrom":subQ5}),-1.0]])]});}
            var Q67;
            {var subQ0=sQuery(id+"F0.wireOp",EDGE,"E21");var subQ1=sQuery(id+"F0.wireOp",EDGE,"E0");var subQ2=makeQuery(id+"F0.imprint","INTERSECT",VERTEX,{"derivedFrom":[subQ1,subQ0]});Q67=makeQuery(id+"F0.imprint","IMPRINT",FACE,{"disambiguationData":[TD([[makeQuery(id+"F0.imprint","IMPRINT",EDGE,{"disambiguationData":[TD([[subQ2,-1.0]])],"derivedFrom":subQ1}),1.0]])]});}
            var Q68;
            {var subQ0=sQuery(id+"F0.wireOp",EDGE,"E26");var subQ1=sQuery(id+"F0.wireOp",EDGE,"E2");var subQ2=makeQuery(id+"F0.imprint","INTERSECT",VERTEX,{"derivedFrom":[subQ1,subQ0]});Q68=makeQuery(id+"F0.imprint","IMPRINT",FACE,{"disambiguationData":[TD([[makeQuery(id+"F0.imprint","IMPRINT",EDGE,{"disambiguationData":[TD([[subQ2,-1.0]])],"derivedFrom":subQ1}),-1.0]])]});}
            extrude(context, id + "F1", {"entities" : qUnion([Q0, Q1, Q2, Q3, Q4, Q5, Q6, Q7, Q8, Q9, Q10, Q11, Q12, Q13, Q14, Q15, Q16, Q17, Q18, Q19, Q20, Q21, Q22, Q23, Q24, Q25, Q26, Q27, Q28, Q29, Q30, Q31, Q32, Q33, Q34, Q35, Q36, Q37, Q38, Q39, Q40, Q41, Q42, Q43, Q44, Q45, Q46, Q47, Q48, Q49, Q50, Q51, Q52, Q53, Q54, Q55, Q56, Q57, Q58, Q59, Q60, Q61, Q62, Q63, Q64, Q65, Q66, Q67, Q68]), "depth" : 1.02 * mm});
        }
        {
            var Q0;
            Q0=makeQuery(id+"F1.opExtrude","CAP_FACE",FACE,{"disambiguationData":[OSD([sQuery(id+"F0.wireOp",EDGE,"E20"),sQuery(id+"F0.wireOp",EDGE,"E21"),sQuery(id+"F0.wireOp",EDGE,"E46"),sQuery(id+"F0.wireOp",EDGE,"E49")])],"isStart":false});
            var sketch = newSketch(context, id + "F2", { "sketchPlane" : qUnion([Q0])});
            skPoint(sketch, "E58.0", {"position": v(38.64, 25.21) * mm});
            skLineSegment(sketch, "E59.0", {"start": v(0, -62.4) * mm, "end": v(38.64, 25.21) * mm});
            skLineSegment(sketch, "E60.0", {"start": v(-30.4, 25.21) * mm, "end": v(0, -62.4) * mm});
            skLineSegment(sketch, "E61.0", {"start": v(-30.4, 25.21) * mm, "end": v(38.64, 25.21) * mm});
            skSolve(sketch);
        }
        {
            var Q0;
            {var subQ0=sQuery(id+"F0.wireOp",EDGE,"E49");var subQ1=sQuery(id+"F0.wireOp",EDGE,"E20");var subQ2=makeQuery(id+"F0.imprint","INTERSECT",VERTEX,{"derivedFrom":[subQ1,subQ0]});Q0=makeQuery(id+"F0.imprint","IMPRINT",FACE,{"disambiguationData":[TD([[makeQuery(id+"F0.imprint","IMPRINT",EDGE,{"disambiguationData":[TD([[subQ2,-1.0]])],"derivedFrom":subQ1}),1.0]])]});}
            var sketch = newSketch(context, id + "F3", { "sketchPlane" : qUnion([Q0])});
            skLineSegment(sketch, "E62.0", {"start": v(0, -62.4) * mm, "end": v(38.64, 25.21) * mm});
            skLineSegment(sketch, "E63.0", {"start": v(-30.4, 25.21) * mm, "end": v(38.64, 25.21) * mm});
            skLineSegment(sketch, "E64.0", {"start": v(-30.4, 25.21) * mm, "end": v(0, -62.4) * mm});
            skSolve(sketch);
        }
        {
            var Q0;
            Q0 = qSketchRegion(id + "F3", true);
            extrude(context, id + "F4", {"entities" : qUnion([Q0]), "oppositeDirection" : true, "depth" : 0.5 * mm});
        }
        {
            var Q0;
            {var subQ0=sQuery(id+"F0.wireOp",EDGE,"E3");Q0=makeQuery(id+"F0.imprint","IMPRINT",FACE,{"disambiguationData":[TD([[makeQuery(id+"F0.imprint","IMPRINT",EDGE,{"derivedFrom":subQ0}),-1.0]])]});}
            var sketch = newSketch(context, id + "F5", { "sketchPlane" : qUnion([Q0])});
            skText(sketch, "E65", { "text": "Brrr", "fontName": "OpenSans-BoldItalic.ttf"});
            const initialGuessF5  = {"E65": [-0.01776, 0.02673, 1, 0, 0.01623]};
            skSetInitialGuess(sketch, initialGuessF5);
            skSolve(sketch);
        }
        {
            var Q0;
            Q0 = qSketchRegion(id + "F5", true);
            extrude(context, id + "F6", {"entities" : qUnion([Q0]), "depth" : 1.52 * mm});
        }
        {
            var Q0;
            {var subQ0=sQuery(id+"F0.wireOp",EDGE,"E3");Q0=makeQuery(id+"F0.imprint","IMPRINT",FACE,{"disambiguationData":[TD([[makeQuery(id+"F0.imprint","IMPRINT",EDGE,{"derivedFrom":subQ0}),-1.0]])]});}
            var sketch = newSketch(context, id + "F7", { "sketchPlane" : qUnion([Q0])});
            skSolve(sketch);
        }
        {
            var Q0;
            {var subQ0=sQuery(id+"F0.wireOp",EDGE,"E3");Q0=makeQuery(id+"F0.imprint","IMPRINT",FACE,{"disambiguationData":[TD([[makeQuery(id+"F0.imprint","IMPRINT",EDGE,{"derivedFrom":subQ0}),-1.0]])]});}
            extrude(context, id + "F8", {"entities" : qUnion([Q0]), "oppositeDirection" : true, "depth" : 0.76 * mm});
        }
        {
            var Q0;
            {var subQ0=sQuery(id+"F0.wireOp",EDGE,"E3");Q0=makeQuery(id+"F7.imprint","IMPRINT",FACE,{"disambiguationData":[TD([[makeQuery(id+"F7.imprint","IMPRINT",EDGE,{"derivedFrom":makeQuery(id+"F0.imprint","IMPRINT",EDGE,{"derivedFrom":subQ0})}),-1.0]])]});}
            var sketch = newSketch(context, id + "F9", { "sketchPlane" : qUnion([Q0])});
            skArc(sketch, "E66", {"start": v(-43.42, 50.83) * mm, "mid": v(-44.91, 43.04) * mm, "end": v(-37.17, 44.8) * mm});
            skArc(sketch, "E67", {"start": v(-37.17, 44.8) * mm, "mid": v(-34.37, 42.8) * mm, "end": v(-31.57, 44.8) * mm});
            skArc(sketch, "E68", {"start": v(-31.57, 44.8) * mm, "mid": v(-27.2, 42.07) * mm, "end": v(-22.8, 44.8) * mm});
            skArc(sketch, "E69", {"start": v(-22.8, 44.8) * mm, "mid": v(-18.15, 41.81) * mm, "end": v(-13.5, 44.8) * mm});
            skArc(sketch, "E70", {"start": v(-13.5, 44.8) * mm, "mid": v(-9.5, 43.28) * mm, "end": v(-5.52, 44.8) * mm});
            skArc(sketch, "E71", {"start": v(-5.52, 44.8) * mm, "mid": v(-0.8, 41.9) * mm, "end": v(3.93, 44.8) * mm});
            skArc(sketch, "E72", {"start": v(3.93, 44.8) * mm, "mid": v(8.18, 43.03) * mm, "end": v(12.43, 44.8) * mm});
            skArc(sketch, "E73", {"start": v(12.43, 44.8) * mm, "mid": v(17.46, 41.62) * mm, "end": v(22.5, 44.8) * mm});
            skArc(sketch, "E74", {"start": v(22.5, 44.8) * mm, "mid": v(27.56, 42.63) * mm, "end": v(32.62, 44.8) * mm});
            skArc(sketch, "E75", {"start": v(32.62, 44.8) * mm, "mid": v(37.27, 41.72) * mm, "end": v(41.92, 44.8) * mm});
            skArc(sketch, "E76", {"start": v(41.92, 44.8) * mm, "mid": v(44.93, 41.08) * mm, "end": v(47.95, 44.8) * mm});
            skArc(sketch, "E77", {"start": v(48, 44.37) * mm, "mid": v(56.33, 42.62) * mm, "end": v(54.12, 50.83) * mm});
            skFitSpline(sketch, "E78", {"points": [v(-43.42, 50.83) * mm, v(-43.42, 69.96) * mm, v(-35.58, 85.57) * mm, v(-20.88, 93.2) * mm, v(-5.6, 92.45) * mm, v(6.62, 83.66) * mm, v(9.86, 69.34) * mm, v(9.86, 58.46) * mm, v(8.18, 49.03) * mm, v(3.93, 44.8) * mm], "startDerivative": vector(-12.93, 147) * mm, "endDerivative": vector(-65.9, -46.89) * mm});
            skSolve(sketch);
        }
        {
            var Q0;
            {var subQ0=sQuery(id+"F9.wireOp",EDGE,"E78");var subQ1=sQuery(id+"F9.wireOp",EDGE,"E66");var subQ2=makeQuery(id+"F9.imprint","INTERSECT",VERTEX,{"derivedFrom":[subQ1,subQ0]});Q0=makeQuery(id+"F9.imprint","IMPRINT",FACE,{"disambiguationData":[TD([[makeQuery(id+"F9.imprint","IMPRINT",EDGE,{"disambiguationData":[TD([[subQ2,-1.0]])],"derivedFrom":subQ1}),1.0]])]});}
            var Q1;
            {var subQ8=sQuery(id+"F9.wireOp",EDGE,"E67");Q1=makeQuery(id+"F9.imprint","IMPRINT",FACE,{"disambiguationData":[TD([[makeQuery(id+"F9.imprint","IMPRINT",EDGE,{"derivedFrom":subQ8}),1.0]])]});}
            var Q2;
            Q2=sQuery(id+"F9.wireOp",EDGE,"E78");
            var Q3;
            Q3=sQuery(id+"F9.wireOp",EDGE,"E66");
            var Q4;
            Q4=sQuery(id+"F9.wireOp",EDGE,"E67");
            var Q5;
            Q5=sQuery(id+"F9.wireOp",EDGE,"E68");
            var Q6;
            Q6=sQuery(id+"F9.wireOp",EDGE,"E69");
            var Q7;
            Q7=sQuery(id+"F9.wireOp",EDGE,"E70");
            var Q8;
            Q8=sQuery(id+"F9.wireOp",EDGE,"E71");
            extrude(context, id + "F10", {"entities" : qUnion([Q0, Q1]), "operationType" : NewBodyOperationType.ADD, "surfaceEntities" : qUnion([Q2, Q3, Q4, Q5, Q6, Q7, Q8]), "depth" : 1.02 * mm});
        }
        {
            var Q0;
            {var subQ0=sQuery(id+"F0.wireOp",EDGE,"E3");Q0=makeQuery(id+"F7.imprint","IMPRINT",FACE,{"disambiguationData":[TD([[makeQuery(id+"F7.imprint","IMPRINT",EDGE,{"derivedFrom":makeQuery(id+"F0.imprint","IMPRINT",EDGE,{"derivedFrom":subQ0})}),-1.0]])]});}
            var sketch = newSketch(context, id + "F11", { "sketchPlane" : qUnion([Q0])});
            skArc(sketch, "E79", {"start": v(4.01, 44.86) * mm, "mid": v(7.44, 42.07) * mm, "end": v(10.87, 44.85) * mm});
            skArc(sketch, "E80", {"start": v(10.87, 44.85) * mm, "mid": v(15.7, 41.77) * mm, "end": v(20.51, 44.85) * mm});
            skArc(sketch, "E81", {"start": v(20.51, 44.85) * mm, "mid": v(25.32, 42.1) * mm, "end": v(30.14, 44.85) * mm});
            skArc(sketch, "E82", {"start": v(30.14, 44.85) * mm, "mid": v(34.34, 41.7) * mm, "end": v(38.54, 44.85) * mm});
            skArc(sketch, "E83", {"start": v(38.54, 44.85) * mm, "mid": v(42.96, 41.93) * mm, "end": v(47.38, 44.85) * mm});
            skArc(sketch, "E84", {"start": v(47.38, 44.85) * mm, "mid": v(49.68, 43.56) * mm, "end": v(51.98, 44.85) * mm});
            skFitSpline(sketch, "E85", {"points": [v(4.01, 44.86) * mm, v(4.01, 60.03) * mm, v(6.52, 72.85) * mm, v(12.64, 82.72) * mm, v(23.81, 88.02) * mm, v(42.2, 87.61) * mm, v(52.85, 78.67) * mm, v(57.45, 65.6) * mm, v(56.65, 55.03) * mm, v(51.98, 44.85) * mm], "startDerivative": vector(-4.23, 129.97) * mm, "endDerivative": vector(-53.36, -98.8) * mm});
            skSolve(sketch);
        }
        {
            var Q0;
            Q0 = qSketchRegion(id + "F11", true);
            extrude(context, id + "F12", {"entities" : qUnion([Q0]), "operationType" : NewBodyOperationType.ADD, "depth" : 1.02 * mm});
        }
        {
            var Q0;
            Q0=makeQuery(id+"F12.boolean.opBoolean","MERGE",FACE,{"derivedFrom":[makeQuery(id+"F10.opExtrude","CAP_FACE",FACE,{"disambiguationData":[OSD([sQuery(id+"F9.wireOp",EDGE,"E66"),sQuery(id+"F9.wireOp",EDGE,"E67"),sQuery(id+"F9.wireOp",EDGE,"E68"),sQuery(id+"F9.wireOp",EDGE,"E69"),sQuery(id+"F9.wireOp",EDGE,"E70"),sQuery(id+"F9.wireOp",EDGE,"E71"),sQuery(id+"F9.wireOp",EDGE,"E78")])],"isStart":false}),makeQuery(id+"F12.opExtrude","CAP_FACE",FACE,{"disambiguationData":[OSD([sQuery(id+"F11.wireOp",EDGE,"E79"),sQuery(id+"F11.wireOp",EDGE,"E80"),sQuery(id+"F11.wireOp",EDGE,"E81"),sQuery(id+"F11.wireOp",EDGE,"E82"),sQuery(id+"F11.wireOp",EDGE,"E83"),sQuery(id+"F11.wireOp",EDGE,"E84"),sQuery(id+"F11.wireOp",EDGE,"E85")])],"isStart":false})]});
            var sketch = newSketch(context, id + "F13", { "sketchPlane" : qUnion([Q0])});
            skLineSegment(sketch, "E86", {"start": v(8.86, 77.9) * mm, "end": v(-12.94, 77.9) * mm});
            skLineSegment(sketch, "E87", {"start": v(8.86, 77.9) * mm, "end": v(29.4, 77.9) * mm});
            skArc(sketch, "E88", {"start": v(-20.15, 81.5) * mm, "mid": v(-19.45, 73.87) * mm, "end": v(-12.94, 77.9) * mm});
            skArc(sketch, "E89", {"start": v(29.4, 77.9) * mm, "mid": v(37.87, 73.18) * mm, "end": v(37.44, 82.86) * mm});
            skArc(sketch, "E90", {"start": v(-12.94, 77.9) * mm, "mid": v(-7.5, 73.73) * mm, "end": v(-2.04, 77.9) * mm});
            skArc(sketch, "E91", {"start": v(-2.04, 77.9) * mm, "mid": v(1.92, 74.46) * mm, "end": v(5.89, 77.9) * mm});
            skArc(sketch, "E92", {"start": v(5.89, 77.9) * mm, "mid": v(10.22, 72.34) * mm, "end": v(14.56, 77.9) * mm});
            skArc(sketch, "E93", {"start": v(14.56, 77.9) * mm, "mid": v(18.83, 73.29) * mm, "end": v(23.1, 77.9) * mm});
            skArc(sketch, "E94", {"start": v(23.1, 77.9) * mm, "mid": v(26.25, 75.34) * mm, "end": v(29.4, 77.9) * mm});
            skFitSpline(sketch, "E95", {"points": [v(-20.15, 81.5) * mm, v(-20.15, 100.18) * mm, v(-13.22, 113.03) * mm, v(-1.84, 121.87) * mm, v(20.2, 122.7) * mm, v(37.65, 112.33) * mm, v(42.65, 97.92) * mm, v(37.44, 82.86) * mm], "startDerivative": vector(-13.24, 131.95) * mm, "endDerivative": vector(-53.73, -108.47) * mm});
            skSolve(sketch);
        }
        {
            var Q0;
            Q0 = qSketchRegion(id + "F13", true);
            extrude(context, id + "F14", {"entities" : qUnion([Q0]), "operationType" : NewBodyOperationType.ADD, "depth" : 1.02 * mm});
        }
        {
            var Q0;
            Q0=makeQuery(id+"F4.opExtrude","CAP_FACE",FACE,{"disambiguationData":[OSD([sQuery(id+"F3.wireOp",EDGE,"E62.0"),sQuery(id+"F3.wireOp",EDGE,"E63.0"),sQuery(id+"F3.wireOp",EDGE,"E64.0")])],"isStart":false});
            extrude(context, id + "F15", {"entities" : qUnion([Q0]), "depth" : 0.25 * mm});
        }
        {
            var Q0;
            Q0=makeQuery(id+"F12.boolean.opBoolean","MERGE",FACE,{"derivedFrom":[makeQuery(id+"F10.opExtrude","CAP_FACE",FACE,{"disambiguationData":[OSD([sQuery(id+"F9.wireOp",EDGE,"E66"),sQuery(id+"F9.wireOp",EDGE,"E67"),sQuery(id+"F9.wireOp",EDGE,"E68"),sQuery(id+"F9.wireOp",EDGE,"E69"),sQuery(id+"F9.wireOp",EDGE,"E70"),sQuery(id+"F9.wireOp",EDGE,"E71"),sQuery(id+"F9.wireOp",EDGE,"E78")])],"isStart":true}),makeQuery(id+"F12.opExtrude","CAP_FACE",FACE,{"disambiguationData":[OSD([sQuery(id+"F11.wireOp",EDGE,"E79"),sQuery(id+"F11.wireOp",EDGE,"E80"),sQuery(id+"F11.wireOp",EDGE,"E81"),sQuery(id+"F11.wireOp",EDGE,"E82"),sQuery(id+"F11.wireOp",EDGE,"E83"),sQuery(id+"F11.wireOp",EDGE,"E84"),sQuery(id+"F11.wireOp",EDGE,"E85")])],"isStart":true})]});
            var Q1;
            Q1=makeQuery(id+"F14.opExtrude","CAP_FACE",FACE,{"disambiguationData":[OSD([sQuery(id+"F13.wireOp",EDGE,"E88"),sQuery(id+"F13.wireOp",EDGE,"E89"),sQuery(id+"F13.wireOp",EDGE,"E90"),sQuery(id+"F13.wireOp",EDGE,"E91"),sQuery(id+"F13.wireOp",EDGE,"E92"),sQuery(id+"F13.wireOp",EDGE,"E93"),sQuery(id+"F13.wireOp",EDGE,"E94"),sQuery(id+"F13.wireOp",EDGE,"E95")])],"isStart":true});
            extrude(context, id + "F16", {"entities" : qUnion([Q0, Q1]), "operationType" : NewBodyOperationType.ADD, "depth" : 0.76 * mm});
        }
        {
            var Q0;
            Q0=makeQuery(id+"F16.opExtrude","CAP_FACE",FACE,{"disambiguationData":[OSD([sQuery(id+"F13.wireOp",EDGE,"E88"),sQuery(id+"F13.wireOp",EDGE,"E89"),sQuery(id+"F13.wireOp",EDGE,"E90"),sQuery(id+"F13.wireOp",EDGE,"E91"),sQuery(id+"F13.wireOp",EDGE,"E92"),sQuery(id+"F13.wireOp",EDGE,"E93"),sQuery(id+"F13.wireOp",EDGE,"E94"),sQuery(id+"F13.wireOp",EDGE,"E95")])],"isStart":false});
            extrude(context, id + "F17", {"entities" : qUnion([Q0]), "operationType" : NewBodyOperationType.ADD, "depth" : 1.02 * mm});
        }
        {
            var Q0;
            Q0=makeQuery(id+"F14.opExtrude","CAP_FACE",FACE,{"disambiguationData":[OSD([sQuery(id+"F13.wireOp",EDGE,"E88"),sQuery(id+"F13.wireOp",EDGE,"E89"),sQuery(id+"F13.wireOp",EDGE,"E90"),sQuery(id+"F13.wireOp",EDGE,"E91"),sQuery(id+"F13.wireOp",EDGE,"E92"),sQuery(id+"F13.wireOp",EDGE,"E93"),sQuery(id+"F13.wireOp",EDGE,"E94"),sQuery(id+"F13.wireOp",EDGE,"E95")])],"isStart":false});
            var sketch = newSketch(context, id + "F18", { "sketchPlane" : qUnion([Q0])});
            skFitSpline(sketch, "E96", {"points": [v(9.9, 123.88) * mm, v(9.4, 129.26) * mm, v(10.5, 131.58) * mm, v(12.84, 131.55) * mm, v(13.52, 129.78) * mm], "startDerivative": vector(-2.76, 17.03) * mm, "endDerivative": vector(1.27, -10.41) * mm});
            skFitSpline(sketch, "E97", {"points": [v(9.9, 123.88) * mm, v(11.22, 123.87) * mm, v(11.07, 129.93) * mm, v(11.5, 130.79) * mm, v(12.17, 130.5) * mm, v(12.4, 129.5) * mm, v(13.52, 129.78) * mm], "startDerivative": vector(10.54, -4.36) * mm, "endDerivative": vector(9.92, 4.91) * mm});
            skSolve(sketch);
        }
        {
            var Q0;
            {var subQ0=sQuery(id+"F18.wireOp",EDGE,"E96");Q0=makeQuery(id+"F18.imprint","IMPRINT",FACE,{"disambiguationData":[TD([[makeQuery(id+"F18.imprint","IMPRINT",EDGE,{"derivedFrom":subQ0}),-1.0]])]});}
            extrude(context, id + "F19", {"entities" : qUnion([Q0]), "operationType" : NewBodyOperationType.ADD, "oppositeDirection" : true, "depth" : 1.27 * mm});
        }
    });
